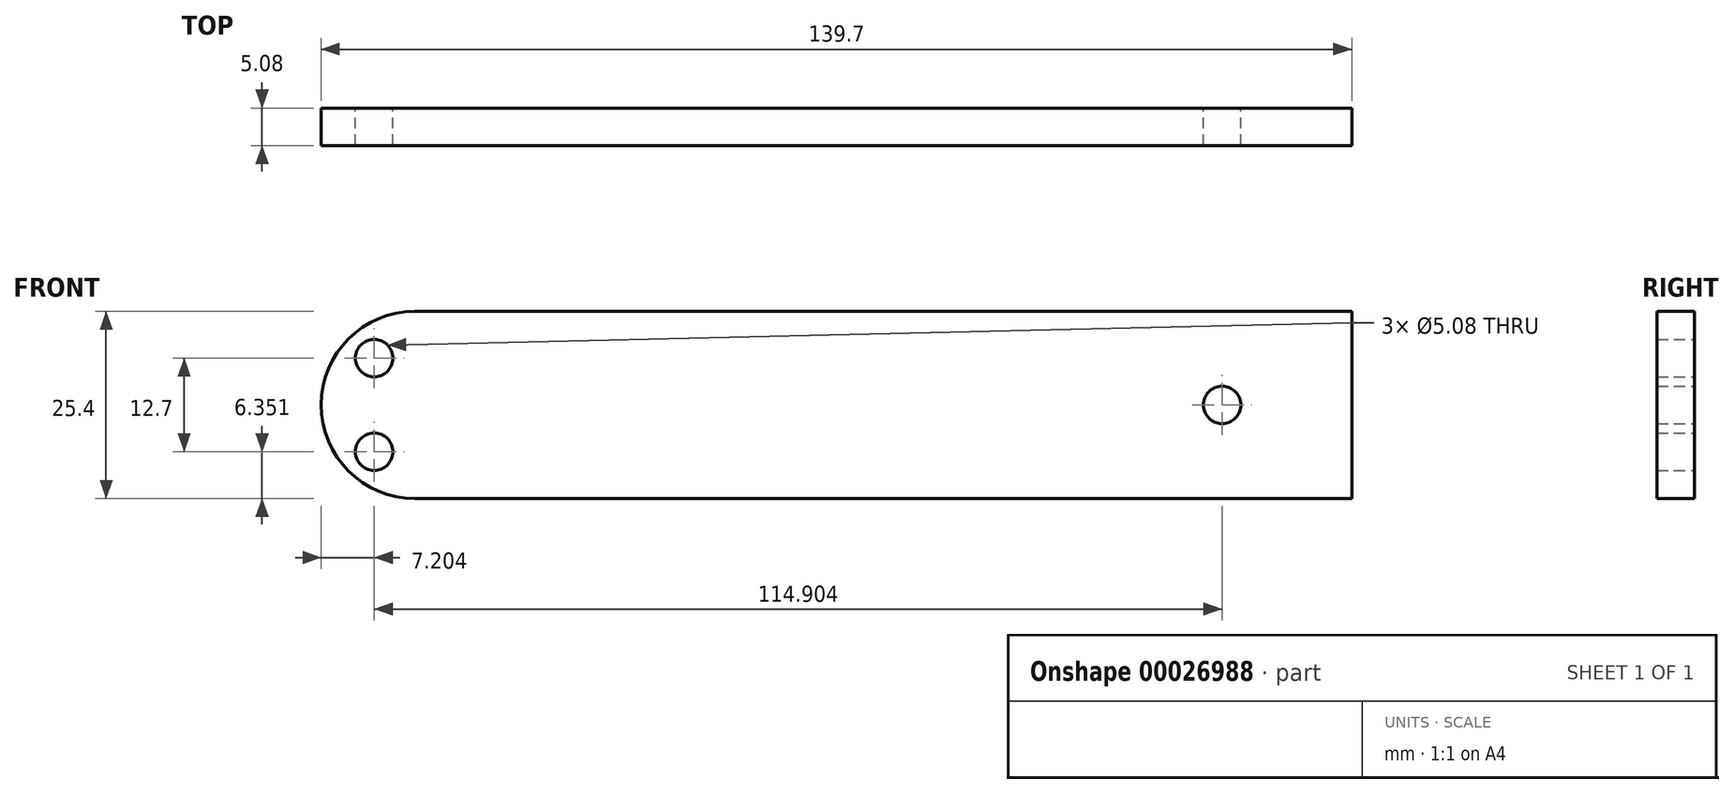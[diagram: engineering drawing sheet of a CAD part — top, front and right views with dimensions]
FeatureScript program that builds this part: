
annotation { "Feature Type Name" : "Feature", "Feature Type Description" : "" }
export const myFeature = defineFeature(function(context is Context, id is Id, definition is map)
    precondition{}
    {
        {
            var Q0;
            Q0=qCreatedBy(makeId("Front.planeOp"),FACE);
            var sketch = newSketch(context, id + "F0", { "sketchPlane" : qUnion([Q0])});
            skLineSegment(sketch, "E0.bottom", {"start": v(-52.15, 27.43) * mm, "end": v(74.85, 27.43) * mm});
            skLineSegment(sketch, "E0.top", {"start": v(-52.15, 2.03) * mm, "end": v(74.85, 2.03) * mm});
            skLineSegment(sketch, "E0.left", {"start": v(-52.15, 27.43) * mm, "end": v(-52.15, 2.03) * mm});
            skLineSegment(sketch, "E0.right", {"start": v(74.85, 27.43) * mm, "end": v(74.85, 2.03) * mm});
            skArc(sketch, "E1", {"start": v(-52.15, 27.43) * mm, "mid": v(-64.85, 14.73) * mm, "end": v(-52.15, 2.03) * mm});
            skPoint(sketch, "E2", {"position": v(-52.15, 21.08) * mm});
            skPoint(sketch, "E3", {"position": v(-52.15, 8.38) * mm});
            skPoint(sketch, "E4", {"position": v(-57.65, 21.08) * mm});
            skPoint(sketch, "E5", {"position": v(-57.65, 8.38) * mm});
            skCircle(sketch, "E6", {"center": v(-57.65, 8.38) * mm, "radius": 2.54 * mm});
            skCircle(sketch, "E7", {"center": v(-57.65, 21.08) * mm, "radius": 2.54 * mm});
            skPoint(sketch, "E8", {"position": v(57.26, 14.73) * mm});
            skCircle(sketch, "E9", {"center": v(57.26, 14.73) * mm, "radius": 2.54 * mm});
            skSolve(sketch);
        }
        {
            var Q0;
            Q0 = qSketchRegion(id + "F0", true);
            extrude(context, id + "F1", {"entities" : qUnion([Q0]), "depth" : 5.08 * mm});
        }
    });
